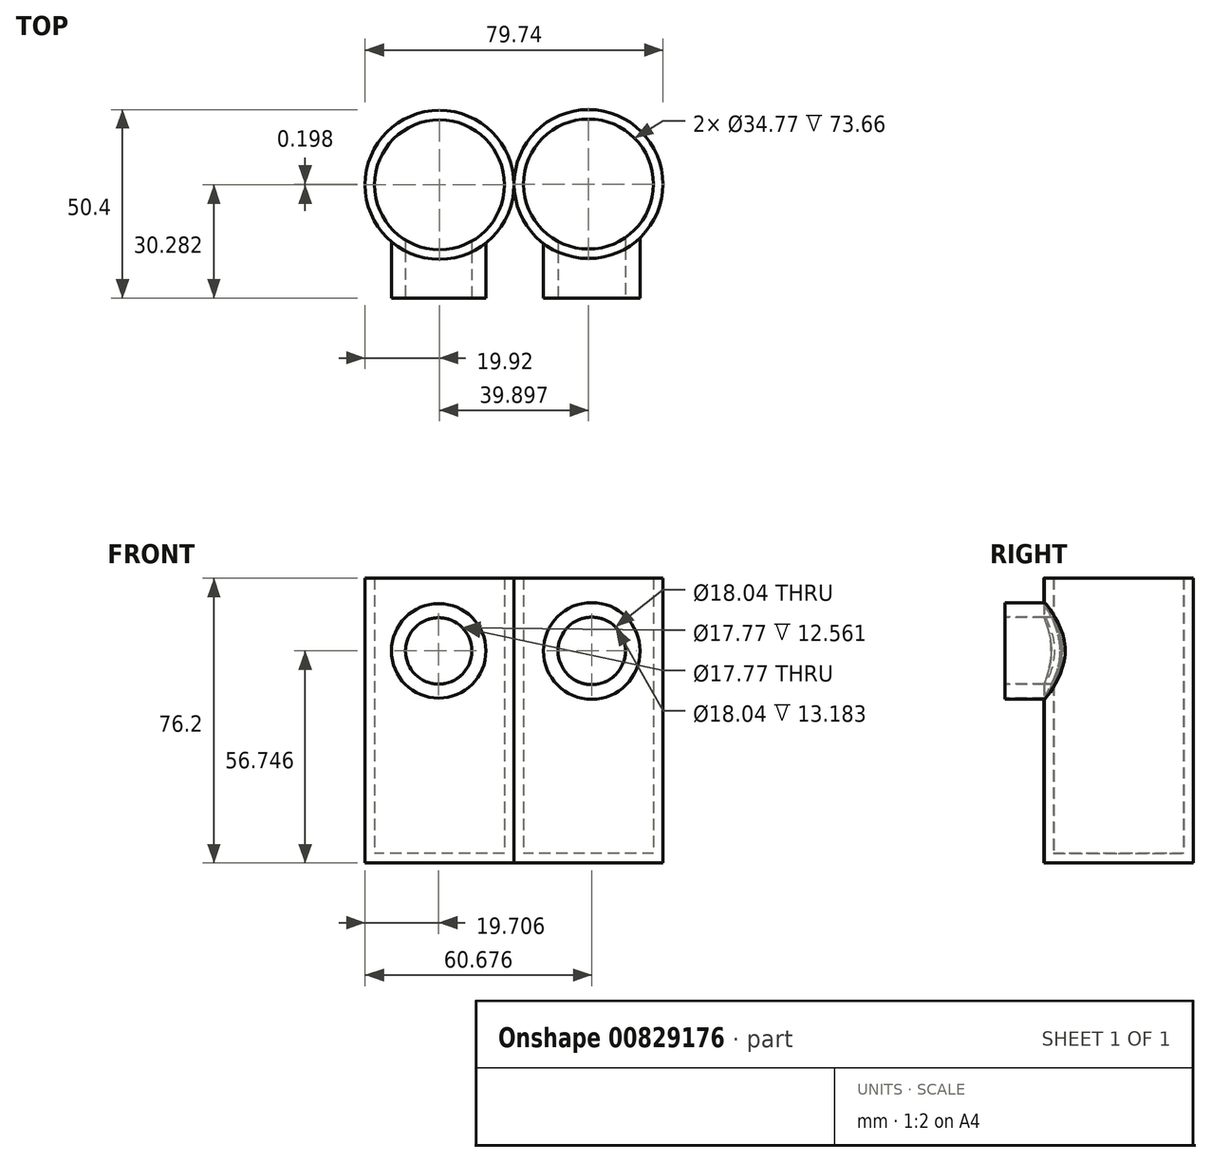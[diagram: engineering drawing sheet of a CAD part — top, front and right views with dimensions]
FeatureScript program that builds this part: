
annotation { "Feature Type Name" : "Feature", "Feature Type Description" : "" }
export const myFeature = defineFeature(function(context is Context, id is Id, definition is map)
    precondition{}
    {
        {
            var Q0;
            Q0=qCreatedBy(makeId("Top.planeOp"),FACE);
            var sketch = newSketch(context, id + "F0", { "sketchPlane" : qUnion([Q0])});
            skCircle(sketch, "E0", {"center": v(20.1, 0) * mm, "radius": 19.92 * mm});
            skSolve(sketch);
        }
        {
            var Q0;
            Q0=qCreatedBy(makeId("Top.planeOp"),FACE);
            var sketch = newSketch(context, id + "F1", { "sketchPlane" : qUnion([Q0])});
            skCircle(sketch, "E1", {"center": v(-19.8, -0.2) * mm, "radius": 19.92 * mm});
            skSolve(sketch);
        }
        {
            var Q0;
            Q0=makeQuery(id+"F1.imprint","IMPRINT",FACE,{"disambiguationData":[TD([[makeQuery(id+"F1.imprint","IMPRINT",EDGE,{"derivedFrom":sQuery(id+"F1.wireOp",EDGE,"E1")}),1.0]])]});
            var Q1;
            Q1=sQuery(id+"F1.wireOp",EDGE,"E1");
            extrude(context, id + "F2", {"entities" : qUnion([Q0]), "surfaceEntities" : qUnion([Q1]), "depth" : 76.2 * mm, "offsetDistance" : 25.4 * mm});
        }
        {
            var Q0;
            Q0=makeQuery(id+"F0.imprint","IMPRINT",FACE,{"disambiguationData":[TD([[makeQuery(id+"F0.imprint","IMPRINT",EDGE,{"derivedFrom":sQuery(id+"F0.wireOp",EDGE,"E0")}),1.0]])]});
            var Q1;
            Q1=sQuery(id+"F0.wireOp",EDGE,"E0");
            extrude(context, id + "F3", {"entities" : qUnion([Q0]), "surfaceEntities" : qUnion([Q1]), "depth" : 76.2 * mm, "offsetDistance" : 25.4 * mm});
        }
        {
            var Q0;
            Q0=makeQuery(id+"F2.opExtrude","CAP_FACE",FACE,{"disambiguationData":[OSD([sQuery(id+"F1.wireOp",EDGE,"E1")])],"isStart":false});
            var Q1;
            Q1=makeQuery(id+"F3.opExtrude","CAP_FACE",FACE,{"disambiguationData":[OSD([sQuery(id+"F0.wireOp",EDGE,"E0")])],"isStart":false});
            shell(context, id + "F4", {"entities" : qUnion([Q0, Q1]), "thickness" : 2.54 * mm});
        }
        {
            var Q0;
            Q0=qCreatedBy(makeId("Front.planeOp"),FACE);
            cPlane(context, id + "F5", {"entities" : qUnion([Q0]), "cplaneType" : CPlaneType.OFFSET, "offset" : 30.48 * mm, "width" : 152.4 * mm, "height" : 152.4 * mm});
        }
        {
            var Q0;
            Q0=qCreatedBy(id+"F5.planeOp",FACE);
            var sketch = newSketch(context, id + "F6", { "sketchPlane" : qUnion([Q0])});
            skCircle(sketch, "E2", {"center": v(20.96, 56.75) * mm, "radius": 12.93 * mm});
            skCircle(sketch, "E3", {"center": v(-20.01, 56.75) * mm, "radius": 12.65 * mm});
            skSolve(sketch);
        }
        {
            var Q0;
            Q0 = qSketchRegion(id + "F6", true);
            extrude(context, id + "F7", {"entities" : qUnion([Q0]), "endBound" : BoundingType.UP_TO_NEXT, "oppositeDirection" : true, "depth" : 25.4 * mm, "offsetDistance" : 25.4 * mm});
        }
        {
            var Q0;
            Q0=makeQuery(id+"F7.opExtrude","CAP_FACE",FACE,{"disambiguationData":[OSD([sQuery(id+"F6.wireOp",EDGE,"E3")])],"isStart":true});
            var sketch = newSketch(context, id + "F8", { "sketchPlane" : qUnion([Q0])});
            skCircle(sketch, "E4", {"center": v(-20.01, 56.75) * mm, "radius": 8.89 * mm});
            skSolve(sketch);
        }
        {
            var Q0;
            Q0 = qSketchRegion(id + "F8", true);
            extrude(context, id + "F9", {"entities" : qUnion([Q0]), "operationType" : NewBodyOperationType.REMOVE, "oppositeDirection" : true, "depth" : 35.05 * mm, "offsetDistance" : 25.4 * mm});
        }
        {
            var Q0;
            Q0=makeQuery(id+"F7.opExtrude","CAP_FACE",FACE,{"disambiguationData":[OSD([sQuery(id+"F6.wireOp",EDGE,"E2")])],"isStart":true});
            var sketch = newSketch(context, id + "F10", { "sketchPlane" : qUnion([Q0])});
            skCircle(sketch, "E5", {"center": v(20.96, 56.75) * mm, "radius": 9.02 * mm});
            skSolve(sketch);
        }
        {
            var Q0;
            Q0 = qSketchRegion(id + "F10", true);
            extrude(context, id + "F11", {"entities" : qUnion([Q0]), "operationType" : NewBodyOperationType.REMOVE, "oppositeDirection" : true, "depth" : 25.4 * mm, "offsetDistance" : 25.4 * mm});
        }
    });
